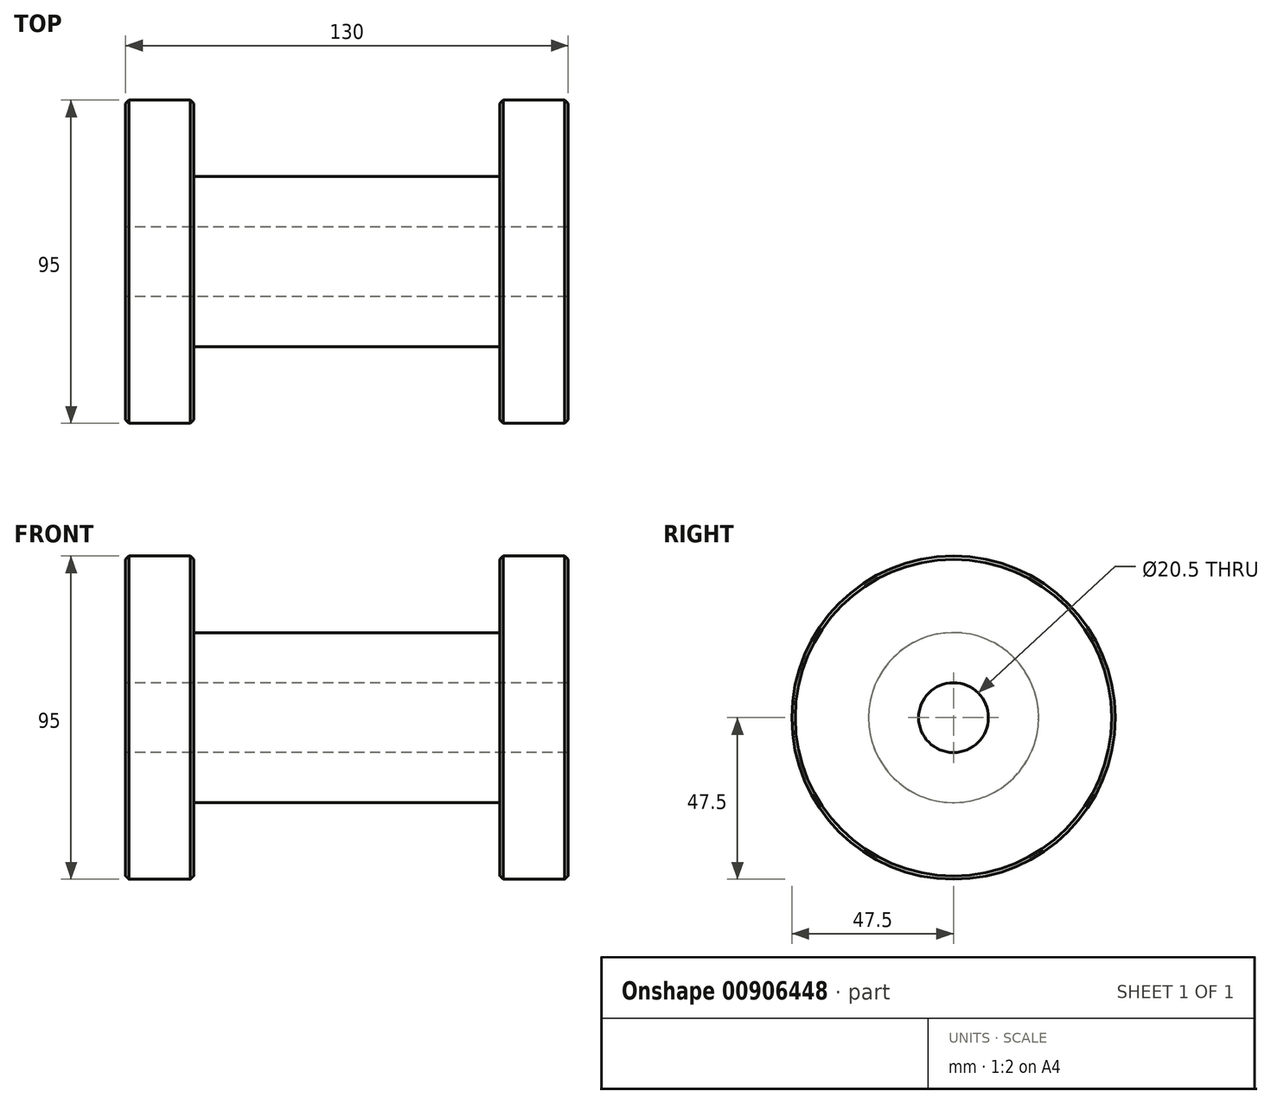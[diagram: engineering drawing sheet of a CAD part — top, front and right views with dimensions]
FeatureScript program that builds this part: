
annotation { "Feature Type Name" : "Feature", "Feature Type Description" : "" }
export const myFeature = defineFeature(function(context is Context, id is Id, definition is map)
    precondition{}
    {
        {
            var Q0;
            Q0=qCreatedBy(makeId("Right.planeOp"),FACE);
            var sketch = newSketch(context, id + "F0", { "sketchPlane" : qUnion([Q0])});
            skCircle(sketch, "E0", {"center": v(0, 0) * mm, "radius": 25 * mm});
            skCircle(sketch, "E1", {"center": v(0, 0) * mm, "radius": 10.25 * mm});
            skSolve(sketch);
        }
        {
            var Q0;
            Q0 = qSketchRegion(id + "F0", true);
            extrude(context, id + "F1", {"entities" : qUnion([Q0]), "endBound" : BoundingType.SYMMETRIC, "depth" : 130 * mm, "offsetDistance" : 25 * mm});
        }
        {
            var Q0;
            Q0=makeQuery(id+"F1.opExtrude","CAP_FACE",FACE,{"disambiguationData":[OSD([sQuery(id+"F0.wireOp",EDGE,"E0"),sQuery(id+"F0.wireOp",EDGE,"E1")])],"isStart":false});
            var sketch = newSketch(context, id + "F2", { "sketchPlane" : qUnion([Q0])});
            skCircle(sketch, "E2", {"center": v(0, 0) * mm, "radius": 25 * mm});
            skCircle(sketch, "E3", {"center": v(0, 0) * mm, "radius": 47.5 * mm});
            skSolve(sketch);
        }
        {
            var Q0;
            Q0 = qSketchRegion(id + "F2", true);
            extrude(context, id + "F3", {"entities" : qUnion([Q0]), "operationType" : NewBodyOperationType.ADD, "oppositeDirection" : true, "depth" : 20 * mm, "offsetDistance" : 25 * mm});
        }
        {
            var Q0;
            Q0=makeQuery(id+"F3.opExtrude","SWEPT_FACE",FACE,{"disambiguationData":[OSD([sQuery(id+"F2.wireOp",EDGE,"E3")])]});
            chamfer(context, id + "F4", {"entities" : qUnion([Q0]), "width" : 1 * mm, "tangentPropagation" : true});
        }
        {
            var Q0;
            Q0=makeQuery(id+"F3.opExtrude","SWEPT_BODY",BODY,{"disambiguationData":[OSD([sQuery(id+"F2.wireOp",EDGE,"E2"),sQuery(id+"F2.wireOp",EDGE,"E3")])]});
            var Q1;
            Q1=makeQuery(id+"F1.opExtrude","SWEPT_BODY",BODY,{"disambiguationData":[OSD([sQuery(id+"F0.wireOp",EDGE,"E0"),sQuery(id+"F0.wireOp",EDGE,"E1")])]});
            var Q2;
            Q2=qCreatedBy(makeId("Right.planeOp"),FACE);
            mirror(context, id + "F5", {"operationType" : NewBodyOperationType.ADD, "entities" : qUnion([Q0, Q1]), "mirrorPlane" : qUnion([Q2])});
        }
    });
